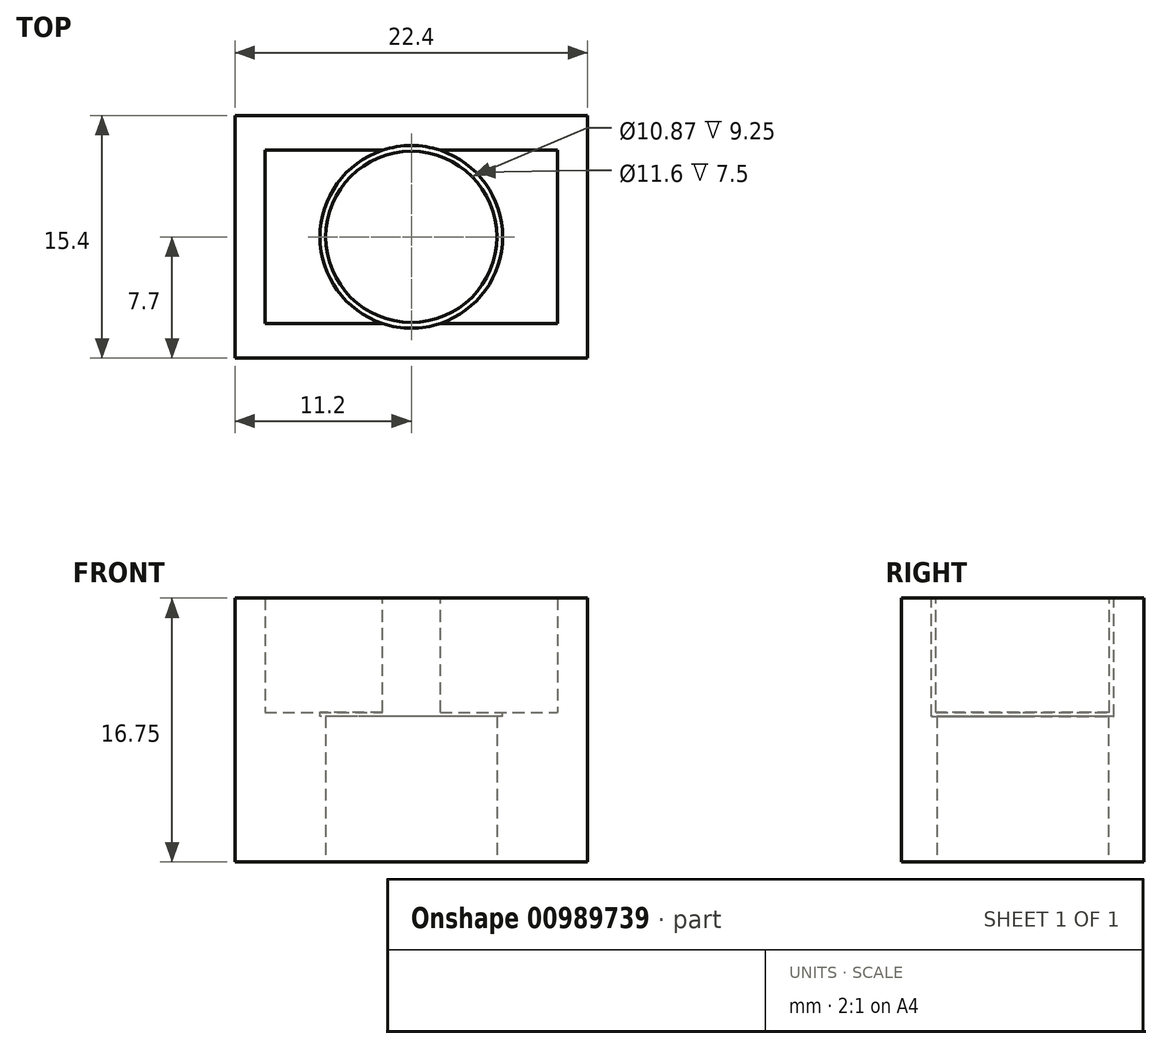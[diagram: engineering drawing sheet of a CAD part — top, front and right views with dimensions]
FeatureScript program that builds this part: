
annotation { "Feature Type Name" : "Feature", "Feature Type Description" : "" }
export const myFeature = defineFeature(function(context is Context, id is Id, definition is map)
    precondition{}
    {
        {
            var Q0;
            Q0=qCreatedBy(makeId("Top.planeOp"),FACE);
            var sketch = newSketch(context, id + "F0", { "sketchPlane" : qUnion([Q0])});
            skLineSegment(sketch, "E0.bottom", {"start": v(-11.2, 7.7) * mm, "end": v(11.2, 7.7) * mm});
            skLineSegment(sketch, "E0.top", {"start": v(-11.2, -7.7) * mm, "end": v(11.2, -7.7) * mm});
            skLineSegment(sketch, "E0.left", {"start": v(-11.2, 7.7) * mm, "end": v(-11.2, -7.7) * mm});
            skLineSegment(sketch, "E0.right", {"start": v(11.2, 7.7) * mm, "end": v(11.2, -7.7) * mm});
            skLineSegment(sketch, "E1.bottom", {"start": v(-9.3, 5.5) * mm, "end": v(9.3, 5.5) * mm});
            skLineSegment(sketch, "E1.top", {"start": v(-9.3, -5.5) * mm, "end": v(9.3, -5.5) * mm});
            skLineSegment(sketch, "E1.left", {"start": v(-9.3, 5.5) * mm, "end": v(-9.3, -5.5) * mm});
            skLineSegment(sketch, "E1.right", {"start": v(9.3, 5.5) * mm, "end": v(9.3, -5.5) * mm});
            skCircle(sketch, "E2", {"center": v(0, 0) * mm, "radius": 5.43 * mm});
            skSolve(sketch);
        }
        {
            var Q0;
            Q0 = qSketchRegion(id + "F0", true);
            extrude(context, id + "F1", {"entities" : qUnion([Q0]), "depth" : 16.75 * mm, "offsetDistance" : 25 * mm});
        }
        {
            var Q0;
            {var subQ0=sQuery(id+"F0.wireOp",EDGE,"E1.left");Q0=makeQuery(id+"F0.imprint","IMPRINT",FACE,{"disambiguationData":[TD([[makeQuery(id+"F0.imprint","IMPRINT",EDGE,{"derivedFrom":subQ0}),1.0]])]});}
            var Q1;
            {var subQ0=sQuery(id+"F0.wireOp",EDGE,"E1.right");Q1=makeQuery(id+"F0.imprint","IMPRINT",FACE,{"disambiguationData":[TD([[makeQuery(id+"F0.imprint","IMPRINT",EDGE,{"derivedFrom":subQ0}),-1.0]])]});}
            extrude(context, id + "F2", {"entities" : qUnion([Q0, Q1]), "operationType" : NewBodyOperationType.ADD, "depth" : 9.5 * mm, "offsetDistance" : 25 * mm});
        }
        {
            var Q0;
            Q0=makeQuery(id+"F1.opExtrude","CAP_FACE",FACE,{"disambiguationData":[OSD([sQuery(id+"F0.wireOp",EDGE,"E0.bottom"),sQuery(id+"F0.wireOp",EDGE,"E0.top"),sQuery(id+"F0.wireOp",EDGE,"E0.left"),sQuery(id+"F0.wireOp",EDGE,"E0.right"),sQuery(id+"F0.wireOp",EDGE,"E1.bottom"),sQuery(id+"F0.wireOp",EDGE,"E1.top"),sQuery(id+"F0.wireOp",EDGE,"E1.left"),sQuery(id+"F0.wireOp",EDGE,"E1.right")])],"isStart":false});
            var sketch = newSketch(context, id + "F3", { "sketchPlane" : qUnion([Q0])});
            skCircle(sketch, "E3", {"center": v(0, 0) * mm, "radius": 5.8 * mm});
            skSolve(sketch);
        }
        {
            var Q0;
            Q0 = qSketchRegion(id + "F3", true);
            extrude(context, id + "F4", {"entities" : qUnion([Q0]), "operationType" : NewBodyOperationType.REMOVE, "oppositeDirection" : true, "depth" : 7.5 * mm, "offsetDistance" : 25 * mm});
        }
    });
